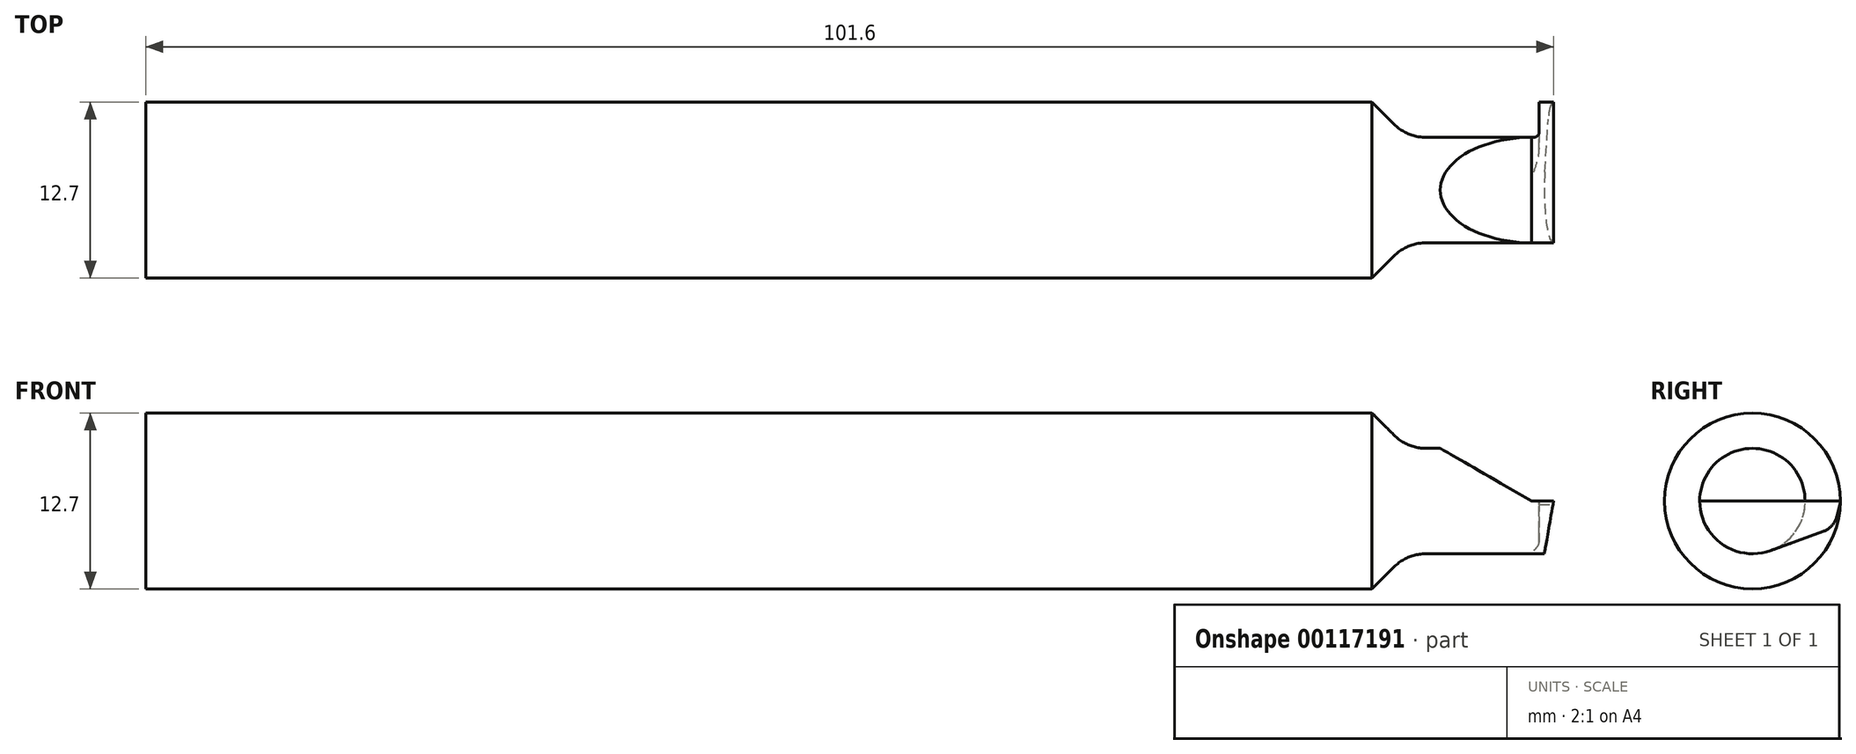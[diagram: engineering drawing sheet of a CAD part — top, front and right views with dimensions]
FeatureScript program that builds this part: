
annotation { "Feature Type Name" : "Feature", "Feature Type Description" : "" }
export const myFeature = defineFeature(function(context is Context, id is Id, definition is map)
    precondition{}
    {
        {
            var Q0;
            Q0=qCreatedBy(makeId("Top.planeOp"),FACE);
            var sketch = newSketch(context, id + "F0", { "sketchPlane" : qUnion([Q0])});
            skLineSegment(sketch, "E0", {"start": v(0, 0) * mm, "end": v(0, 6.35) * mm});
            skLineSegment(sketch, "E1", {"start": v(0, 6.35) * mm, "end": v(-1.04, 6.35) * mm});
            skLineSegment(sketch, "E2", {"start": v(-1.04, 6.35) * mm, "end": v(-1.04, 4.2) * mm});
            skLineSegment(sketch, "E3", {"start": v(-1.42, 3.81) * mm, "end": v(-9.25, 3.81) * mm});
            skLineSegment(sketch, "E4", {"start": v(-11.5, 4.74) * mm, "end": v(-13.1, 6.35) * mm});
            skLineSegment(sketch, "E5", {"start": v(-13.1, 6.35) * mm, "end": v(-101.6, 6.35) * mm});
            skLineSegment(sketch, "E6", {"start": v(-101.6, 6.35) * mm, "end": v(-101.6, 0) * mm});
            skLineSegment(sketch, "E7", {"start": v(-101.6, 0) * mm, "end": v(0, 0) * mm});
            skPoint(sketch, "E8.visualSharp", {"position": v(0, 6.35) * mm});
            skPoint(sketch, "E9.visualSharp", {"position": v(-1.04, 6.35) * mm});
            skPoint(sketch, "E10.visualSharp", {"position": v(-1.04, 3.81) * mm});
            skArc(sketch, "E10.filletArc", {"start": v(-1.42, 3.81) * mm, "mid": v(-1.15, 3.92) * mm, "end": v(-1.04, 4.2) * mm});
            skPoint(sketch, "E11.visualSharp", {"position": v(-10.57, 3.81) * mm});
            skArc(sketch, "E11.filletArc", {"start": v(-11.5, 4.74) * mm, "mid": v(-10.47, 4.05) * mm, "end": v(-9.25, 3.81) * mm});
            skSolve(sketch);
        }
        {
            var Q0;
            Q0 = qSketchRegion(id + "F0", true);
            var Q1;
            Q1=sQuery(id+"F0.wireOp",EDGE,"E7");
            revolve(context, id + "F1", {"entities" : qUnion([Q0]), "axis" : qUnion([Q1]), "revolveType" : RevolveType.FULL});
        }
        {
            var Q0;
            Q0=qCreatedBy(makeId("Front.planeOp"),FACE);
            var sketch = newSketch(context, id + "F2", { "sketchPlane" : qUnion([Q0])});
            skLineSegment(sketch, "E12", {"start": v(0, 0) * mm, "end": v(-1.59, 0) * mm});
            skLineSegment(sketch, "E13", {"start": v(-1.59, 0) * mm, "end": v(-12.59, 6.35) * mm});
            skLineSegment(sketch, "E14", {"start": v(-12.59, 6.35) * mm, "end": v(0, 6.35) * mm});
            skLineSegment(sketch, "E15", {"start": v(0, 6.35) * mm, "end": v(0, 0) * mm});
            skSolve(sketch);
        }
        {
            var Q0;
            Q0 = qSketchRegion(id + "F2", true);
            extrude(context, id + "F3", {"entities" : qUnion([Q0]), "operationType" : NewBodyOperationType.REMOVE, "endBound" : BoundingType.SYMMETRIC, "oppositeDirection" : true, "depth" : 25.4 * mm});
        }
        {
            var Q0;
            Q0=makeQuery(id+"F1.opRevolve","SWEPT_FACE",FACE,{"disambiguationData":[OSD([sQuery(id+"F0.wireOp",EDGE,"E0")])]});
            var sketch = newSketch(context, id + "F4", { "sketchPlane" : qUnion([Q0])});
            skLineSegment(sketch, "E16", {"start": v(-6.6, -6.6) * mm, "end": v(6.35, -6.6) * mm});
            skLineSegment(sketch, "E17", {"start": v(-3.81, 0) * mm, "end": v(-6.6, 0) * mm});
            skLineSegment(sketch, "E18", {"start": v(-6.6, 0) * mm, "end": v(-6.6, -6.6) * mm});
            skLineSegment(sketch, "E19", {"start": v(1.3, -3.58) * mm, "end": v(5.1, -2.2) * mm});
            skLineSegment(sketch, "E20", {"start": v(6.1, -1.12) * mm, "end": v(6.33, -0.25) * mm});
            skLineSegment(sketch, "E21", {"start": v(6.33, -0.25) * mm, "end": v(6.35, 0) * mm});
            skLineSegment(sketch, "E22", {"start": v(6.35, 0) * mm, "end": v(6.35, -6.6) * mm});
            skArc(sketch, "E23.trimOffspring", {"start": v(1.3, -3.58) * mm, "mid": v(-2.19, -3.12) * mm, "end": v(-3.81, 0) * mm});
            skPoint(sketch, "E24.0.start.orphan", {"position": v(3.81, 0) * mm});
            skPoint(sketch, "E25.orphan", {"position": v(-3.81, 0) * mm});
            skPoint(sketch, "E26.visualSharp", {"position": v(5.88, -1.91) * mm});
            skArc(sketch, "E26.filletArc", {"start": v(5.1, -2.2) * mm, "mid": v(5.73, -1.78) * mm, "end": v(6.1, -1.12) * mm});
            skSolve(sketch);
        }
        {
            var Q0;
            {var subQ1=sQuery(id+"F4.wireOp",EDGE,"E19");Q0=makeQuery(id+"F4.imprint","IMPRINT",FACE,{"disambiguationData":[TD([[makeQuery(id+"F4.imprint","IMPRINT",EDGE,{"derivedFrom":subQ1}),-1.0]])]});}
            var Q1;
            Q1=makeQuery(id+"F4.imprint","IMPRINT",FACE,{"disambiguationData":[TD([[makeQuery(id+"F4.imprint","IMPRINT",EDGE,{"derivedFrom":sQuery(id+"F4.wireOp",EDGE,"E16")}),1.0]])]});
            extrude(context, id + "F5", {"entities" : qUnion([Q0, Q1]), "operationType" : NewBodyOperationType.REMOVE, "oppositeDirection" : true, "depth" : 1.59 * mm});
        }
        {
            var Q0;
            Q0=qCreatedBy(makeId("Front.planeOp"),FACE);
            var sketch = newSketch(context, id + "F6", { "sketchPlane" : qUnion([Q0])});
            skLineSegment(sketch, "E27", {"start": v(0, 0) * mm, "end": v(-0.75, -4.24) * mm});
            skLineSegment(sketch, "E28", {"start": v(-0.75, -4.24) * mm, "end": v(0, -4.24) * mm});
            skLineSegment(sketch, "E29", {"start": v(0, -4.24) * mm, "end": v(0, 0) * mm});
            skSolve(sketch);
        }
        {
            var Q0;
            Q0 = qSketchRegion(id + "F6", true);
            extrude(context, id + "F7", {"entities" : qUnion([Q0]), "operationType" : NewBodyOperationType.REMOVE, "endBound" : BoundingType.SYMMETRIC, "oppositeDirection" : true, "depth" : 25.4 * mm});
        }
    });
